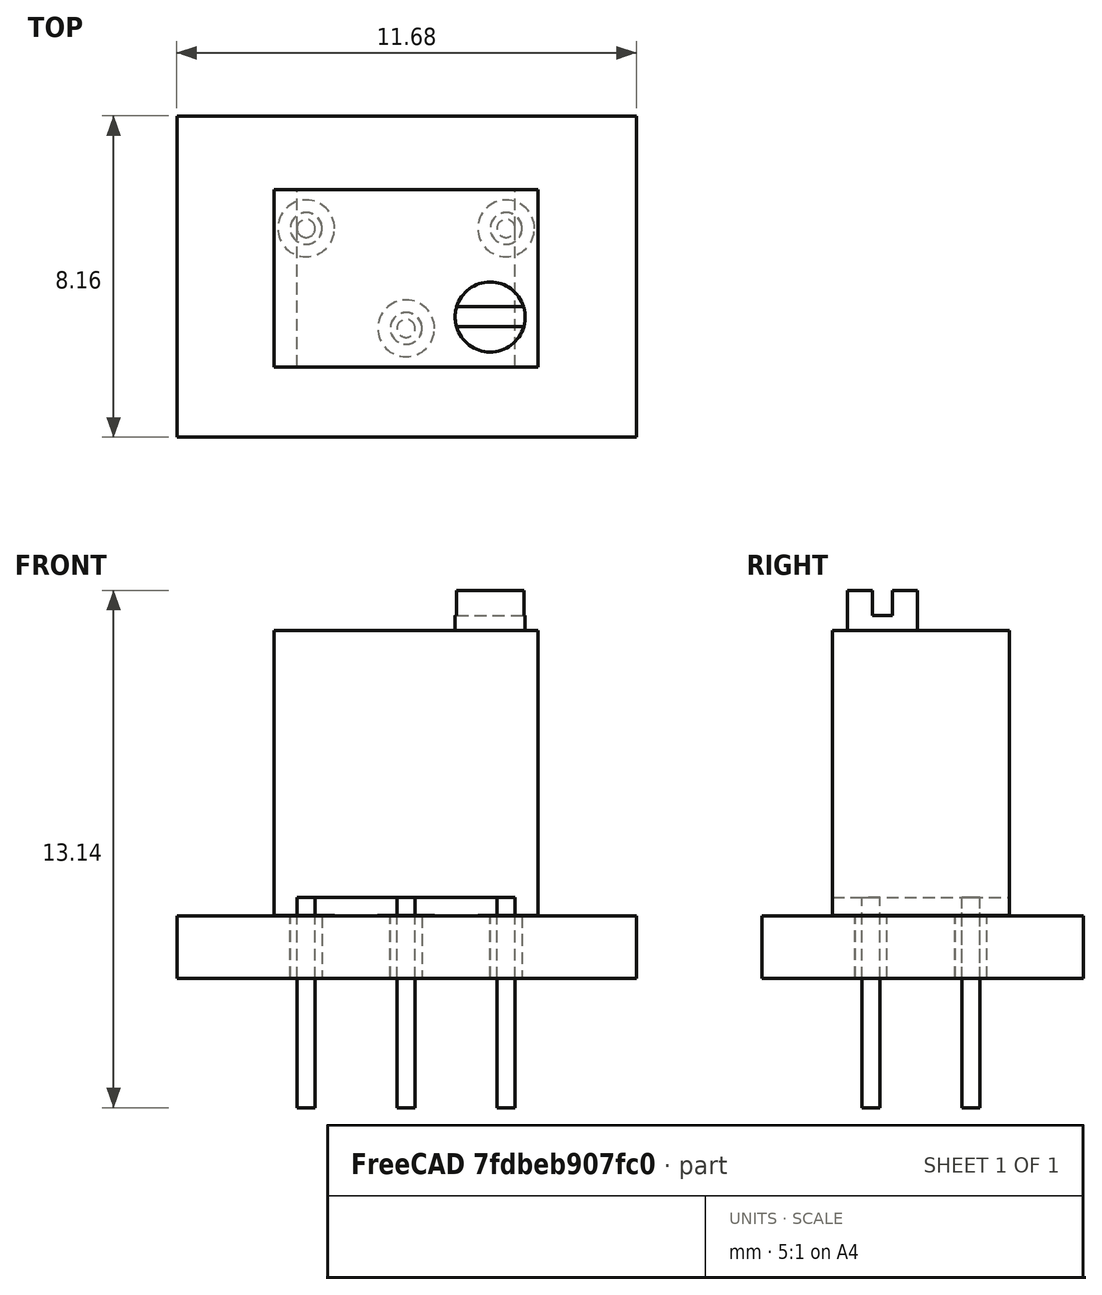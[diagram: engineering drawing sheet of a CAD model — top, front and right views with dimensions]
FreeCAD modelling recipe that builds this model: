
FCSTD DOCUMENT  (FreeCAD 0.18R15611 (Git))
Label: Potentiometer_Bourns_3266W_Vertical
License: All rights reserved
LicenseURL: http://en.wikipedia.org/wiki/All_rights_reserved
objects: Part::FeaturePython×7, Part::Cylinder×4, Part::Box×4, Part::MultiFuse×2, App::DocumentObjectGroup×1, Part::Cut×1, Part::Feature×1
note: 19 computed .brp shape members not serialized (recipe doc carries the construction recipe); baked Part::Feature solids carry a one-line shape summary decoded from their .brp

FEATURE [Part::FeaturePython] FCrtYd_lines  label="FCrtYd"  # a2plus imported part (geometry in sourceFile) (typed FeaturePython)
  fixedPosition = true
FEATURE [Part::FeaturePython] FFab_lines  label="FFab"  # a2plus imported part (geometry in sourceFile) (typed FeaturePython)
  fixedPosition = true
FEATURE [Part::FeaturePython] Filk_lines  label="FrontSilk"  # a2plus imported part (geometry in sourceFile) (typed FeaturePython)
  fixedPosition = true
FEATURE [Part::FeaturePython] TopPads  # a2plus imported part (geometry in sourceFile) (typed FeaturePython)
  fixedPosition = true
FEATURE [Part::FeaturePython] BotPads  # a2plus imported part (geometry in sourceFile) (typed FeaturePython)
  fixedPosition = true
FEATURE [Part::FeaturePython] THPs  label="PTHs"  # a2plus imported part (geometry in sourceFile) (typed FeaturePython)
  fixedPosition = true
FEATURE [Part::FeaturePython] newPCB  label="Pcb"  # a2plus imported part (geometry in sourceFile) (typed FeaturePython)
  fixedPosition = true
FEATURE [App::DocumentObjectGroup] Potentiometer_Bourns_3266W_Vertical_fp
  Group = -> [FCrtYd_lines,FFab_lines,Filk_lines,TopPads,BotPads,THPs,newPCB]
FEATURE [Part::Cylinder] Cylinder  label="Pin1"
  Angle = 360
  AttacherType = Attacher::AttachEngine3D
  Height = 5.34
  Placement = pos=(0,0,-4.88) rot=(0,0,1;0rad)
  Radius = 0.23
FEATURE [Part::Cylinder] Cylinder001  label="Pin3"
  Angle = 360
  AttacherType = Attacher::AttachEngine3D
  Height = 5.34
  Placement = pos=(-5.08,0,-4.88) rot=(0,0,1;0rad)
  Radius = 0.23
FEATURE [Part::Cylinder] Cylinder002  label="Pin2"
  Angle = 360
  AttacherType = Attacher::AttachEngine3D
  Height = 5.34
  Placement = pos=(-2.54,-2.54,-4.88) rot=(0,0,1;0rad)
  Radius = 0.23
FEATURE [Part::Box] Box  label="Body"
  AttacherType = Attacher::AttachEngine3D
  Height = 6.78
  Length = 6.71
  Placement = pos=(-5.895,-3.52,0.46) rot=(0,0,1;0rad)
  Width = 4.5
FEATURE [Part::Box] Box001  label="Standoff1"
  AttacherType = Attacher::AttachEngine3D
  Height = 0.46
  Length = 0.585
  Placement = pos=(0.23,-3.52,0) rot=(0,0,1;0rad)
  Width = 4.5
FEATURE [Part::Box] Box002  label="Standoff2"
  AttacherType = Attacher::AttachEngine3D
  Height = 0.46
  Length = 0.585
  Placement = pos=(-5.895,-3.52,0) rot=(0,0,1;0rad)
  Width = 4.5
FEATURE [Part::MultiFuse] Fusion  label="FusionBody"
  Refine = true
  Shapes = -> [Box,Box001,Box002]
FEATURE [Part::Cylinder] Cylinder003  label="Knob"
  Angle = 360
  AttacherType = Attacher::AttachEngine3D
  Height = 1.02
  Placement = pos=(-0.405,-2.25,7.24) rot=(0,0,1;0rad)
  Radius = 0.89
FEATURE [Part::Box] Box003  label="Cube"
  AttacherType = Attacher::AttachEngine3D
  Height = 0.64
  Length = 10
  Placement = pos=(-5,-2.5,7.62) rot=(0,0,1;0rad)
  Width = 0.51
FEATURE [Part::Cut] Cut  label="CutKnob"
  Base = -> Cylinder003
  Refine = true
  Tool = -> Box003
FEATURE [Part::MultiFuse] Pin3_mp_cp  label="Pin3_fd"
  Refine = true
  Shapes = -> [Cylinder001,Cylinder002,Cylinder,Fusion,Cut]
FEATURE [Part::Feature] Shape  label="Potentiometer_Bourns_3266W_Vertical"
  shape: bbox 6.71 x 4.5 x 13.14 mm, 22 faces (baked)
